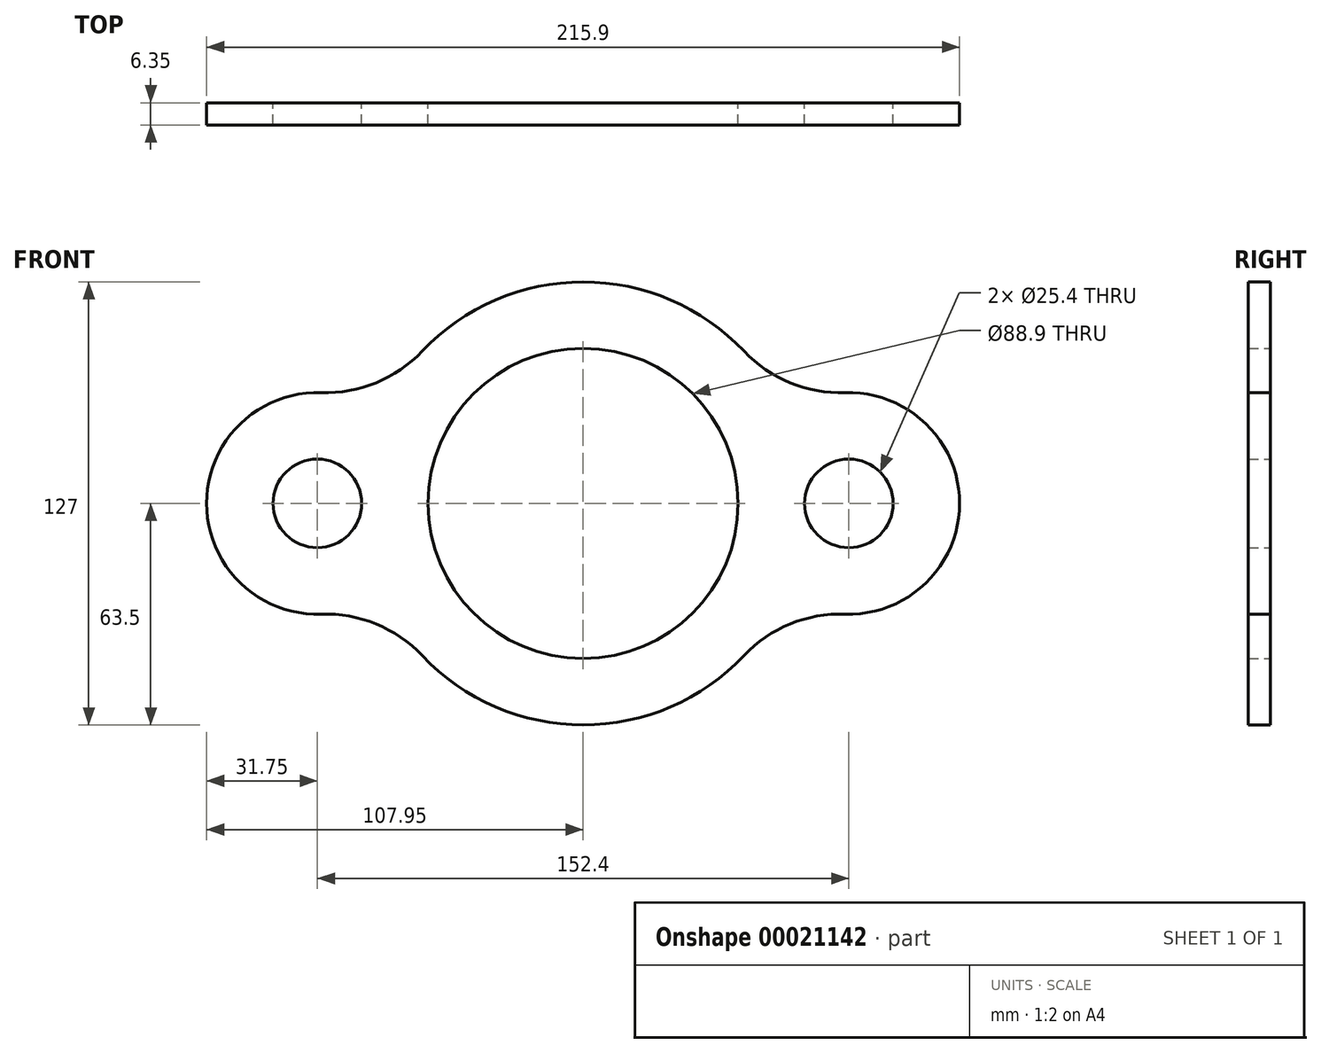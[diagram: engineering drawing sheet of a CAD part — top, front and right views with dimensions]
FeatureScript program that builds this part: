
annotation { "Feature Type Name" : "Feature", "Feature Type Description" : "" }
export const myFeature = defineFeature(function(context is Context, id is Id, definition is map)
    precondition{}
    {
        {
            var Q0;
            Q0=qCreatedBy(makeId("Front.planeOp"),FACE);
            var sketch = newSketch(context, id + "F0", { "sketchPlane" : qUnion([Q0])});
            skCircle(sketch, "E0", {"center": v(0, 0) * mm, "radius": 44.45 * mm});
            skArc(sketch, "E1", {"start": v(-46.14, -43.63) * mm, "mid": v(0, -63.5) * mm, "end": v(46.14, -43.63) * mm});
            skCircle(sketch, "E2", {"center": v(-76.2, 0) * mm, "radius": 12.7 * mm});
            skCircle(sketch, "E3", {"center": v(76.2, 0) * mm, "radius": 12.7 * mm});
            skArc(sketch, "E4", {"start": v(-75.12, 31.73) * mm, "mid": v(-107.95, 0) * mm, "end": v(-75.12, -31.73) * mm});
            skArc(sketch, "E5", {"start": v(75.12, -31.73) * mm, "mid": v(107.95, 0) * mm, "end": v(75.12, 31.73) * mm});
            skArc(sketch, "E6.trimOffspring", {"start": v(46.14, 43.63) * mm, "mid": v(0, 63.5) * mm, "end": v(-46.14, 43.63) * mm});
            skArc(sketch, "E7.filletArc", {"start": v(-75.12, 31.73) * mm, "mid": v(-59.35, 34.56) * mm, "end": v(-46.14, 43.63) * mm});
            skArc(sketch, "E8.filletArc", {"start": v(-46.14, -43.63) * mm, "mid": v(-59.35, -34.56) * mm, "end": v(-75.12, -31.73) * mm});
            skArc(sketch, "E9.filletArc", {"start": v(46.14, 43.63) * mm, "mid": v(59.35, 34.56) * mm, "end": v(75.12, 31.73) * mm});
            skArc(sketch, "E10.filletArc", {"start": v(75.12, -31.73) * mm, "mid": v(59.35, -34.56) * mm, "end": v(46.14, -43.63) * mm});
            skSolve(sketch);
        }
        {
            var Q0;
            Q0=makeQuery(id+"F0.imprint","IMPRINT",FACE,{"disambiguationData":[TD([[makeQuery(id+"F0.imprint","IMPRINT",EDGE,{"derivedFrom":sQuery(id+"F0.wireOp",EDGE,"E0")}),-1.0]])]});
            extrude(context, id + "F1", {"entities" : qUnion([Q0]), "depth" : 6.35 * mm});
        }
    });
